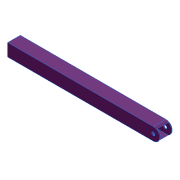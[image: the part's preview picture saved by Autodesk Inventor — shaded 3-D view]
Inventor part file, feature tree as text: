
AUTODESK INVENTOR PART (.ipt)
format: ipt  version: 2012 (Build 160160000, 160)  size: 88,064 bytes
history: native  units: in
note: dims shown in document units (in); Inventor stores cm internally (conversion verified against a paired STEP export)
features: extrude x2, sketch x2, shell x1, fillet x1
ambient origin geometry x8: Origin, YZ Plane, XZ Plane, XY Plane, X Axis, Y Axis, Z Axis, Center Point
bodies: Solid1 (feature_tree)
feature tree (6):
  extrude  "Extrusion1"  Depth=12.0in
  shell  "Shell1"  Thickness=1.0in
  extrude  "Extrusion2"  Depth=0.5in
  fillet  "Fillet1"  Radius=0.5in
  sketch  "Sketch1"  dims[d0=1.0in d1=12.0in d2=1.0in d3=0.0in]
  sketch  "Sketch2"  dims[d4=0.0625in d5=0.5in d6=0.5in d7=0.25in d8=1.0in d9=0.0in d10=0.5in]
